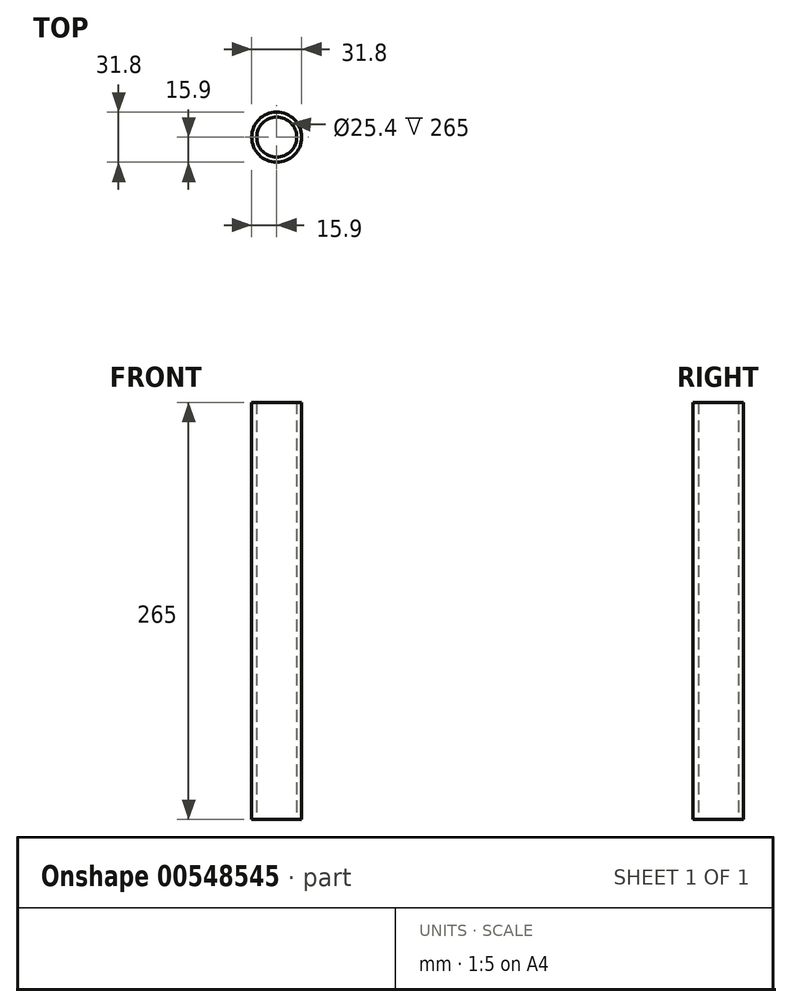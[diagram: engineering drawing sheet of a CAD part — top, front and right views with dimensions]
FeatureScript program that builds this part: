
annotation { "Feature Type Name" : "Feature", "Feature Type Description" : "" }
export const myFeature = defineFeature(function(context is Context, id is Id, definition is map)
    precondition{}
    {
        {
            var Q0;
            Q0=qCreatedBy(makeId("Top.planeOp"),FACE);
            var sketch = newSketch(context, id + "F0", { "sketchPlane" : qUnion([Q0])});
            skCircle(sketch, "E0", {"center": v(0, 0) * mm, "radius": 15.9 * mm});
            skCircle(sketch, "E1", {"center": v(0, 0) * mm, "radius": 12.7 * mm});
            skSolve(sketch);
        }
        {
            var Q0;
            Q0=makeQuery(id+"F0.imprint","IMPRINT",FACE,{"disambiguationData":[TD([[makeQuery(id+"F0.imprint","IMPRINT",EDGE,{"derivedFrom":sQuery(id+"F0.wireOp",EDGE,"E0")}),1.0]])]});
            extrude(context, id + "F1", {"entities" : qUnion([Q0]), "depth" : 265 * mm, "offsetDistance" : 25 * mm});
        }
    });
